# Revit family: Hager-Orion_Plus-IP65-D300-Cl.II-Poly_double_encl-630A-Floor_installation-CH-it
name_source: partatom
category: Electrical Equipment
units: mm (PartAtom-declared; Revit-internal decimal feet)

## family parameters
Cut with Voids When Loaded = No
Host = Face
Panel Configuration = Two Columns, Circuits Across
Part Type = Panelboard
Room Calculation Point = No
Round Connector Dimension = Use Diameter
Shared = No

## types (15) — shared parameters
EF000003 - Tipo di montaggio = EV012274 - montaggio a pavimento
EF000007 - colore = EV000270 - grigio
EF000049 - profondità = 300 mm  [stored 0.984252 ft]
EF000116 - numero RAL = 7035
EF001131 - profondità interna = 300 mm  [stored 0.984252 ft]
EF001596 - Attacco Lampada = EV000139 - plastica
EF001613 - Integrità del circuito = EV000494 - senza
EF005474 - grado di protezione (IP) = EV006421 - IP65
EF006306 - con serratura = Yes
EF007800 - adatto per parafulmine = No
EF008873 - corrente nominale (In) = 630 A
EF009170 - spessore materiale scatola = 2 mm  [stored 0.00656168 ft]
EF009171 - spessore materiale porta/coperchio = 2 mm  [stored 0.00656168 ft]
EF015940 - Coprire con rilascio di sovrapressione = No
HG000003 - Gamma = Orion Plus
HG000006 - Ad incasso = No
HG000010 - Porte asimmetriche = No
HG000023 - Custodia a doppia sezione = Yes
HG000024 - Altezza della sezione inferiore = 800 mm  [stored 2.62467 ft]
HG000026 - A pavimento = Yes
HG000027 - Altezza dello zoccolo = 70 mm  [stored 0.229659 ft]
Manufacturer = Hager
Type Comments = Orion Plus
zero-valued in all types: Default Elevation, EF000218 - profondità di incasso, EF000437 - numero di ingressi per conduttori, EF009554 - numero delle aperture per la piastra della flangia

## per-type parameters (varying)
| type | EF000008 - Larghezza | EF000040 - Altezza | EF000118 - con piastra di montaggio | EF000266 - numero di file | EF000339 - tipo di copertura | EF001088 - possibilità di applicazione | EF002950 - Numero moduli DIN | EF003532 - adatto per uso esterno | EF004293 - resistenza agli urti | EF004427 - numero di moduli | EF004464 - tipo di porta | EF006244 - coperchio/porta trasparente | EF009212 - esecuzione coperchio | HG000002 - Con porta | HG000004 - Codice produttore | HG000009 - Porta doppia a battente |
| montaggio a pavimento IP65 L1100 A1150 P300  - FL360B | 1100 mm | 1150 mm | No | 3 | EV004216 - porta | Yes | 0 | Yes | EV008784 - IK10 | 138 | EV002646 - singolo | Yes | EV009916 - con taglio | Yes | FL360B | Yes |
| montaggio a pavimento IP65 L1100 A1450 P300  - FL362B | 1100 mm | 1450 mm  [stored 4.75722 ft] | No | 3 | EV004216 - porta | Yes | 0 | Yes | EV008784 - IK10 | 138 | EV002646 - singolo | Yes | EV009916 - con taglio | Yes | FL362B | Yes |
| montaggio a pavimento IP65 L1100 A1750 P300  - FL364B | 1100 mm | 1750 mm  [stored 5.74147 ft] | No | 3 | EV004216 - porta | Yes | 0 | Yes | EV008784 - IK10 | 138 | EV002646 - singolo | Yes | EV009916 - con taglio | Yes | FL364B | Yes |
| montaggio a pavimento IP65 L1100 A1750 P300  - FL366B | 1100 mm | 1750 mm  [stored 5.74147 ft] | No | 5 | EV004216 - porta | Yes | 0 | Yes | EV008784 - IK10 | 230 | EV002646 - singolo | Yes | EV009916 - con taglio | Yes | FL366B | Yes |
| montaggio a pavimento IP65 L1100 A2050 P300  - FL368B | 1100 mm | 2050 mm  [stored 6.72572 ft] | Yes | 5 | EV001012 - coperchio | No | 0 | No | EV006814 - IK08 | 230 | EV002646 - singolo | No | EV000116 - chiuso | Yes | FL368B | Yes |
| montaggio a pavimento IP65 L600 A1150 P300  - FL340B | 600 mm | 1150 mm | No | 3 | EV004216 - porta | Yes | 0 | Yes | EV008784 - IK10 | 69 | EV002646 - singolo | Yes | EV009916 - con taglio | Yes | FL340B | No |
| montaggio a pavimento IP65 L600 A1450 P300  - FL342B | 600 mm | 1450 mm  [stored 4.75722 ft] | No | 3 | EV004216 - porta | Yes | 0 | Yes | EV008784 - IK10 | 69 | EV002646 - singolo | Yes | EV009916 - con taglio | No | FL342B | No |
| montaggio a pavimento IP65 L600 A1750 P300  - FL344B | 600 mm | 1750 mm  [stored 5.74147 ft] | No | 9 | EV004216 - porta | Yes | 23 | No |  | 0 |  | Yes | EV009916 - con taglio | Yes | FL344B | No |
| montaggio a pavimento IP65 L600 A1750 P300  - FL346B | 600 mm | 1750 mm  [stored 5.74147 ft] | No | 5 | EV004216 - porta | Yes | 0 | Yes | EV008784 - IK10 | 115 | EV002646 - singolo | Yes | EV009916 - con taglio | Yes | FL346B | No |
| montaggio a pavimento IP65 L600 A2050 P300  - FL348B | 600 mm | 2050 mm  [stored 6.72572 ft] | No | 3 | EV004216 - porta | Yes | 0 | Yes | EV008784 - IK10 | 115 | EV002646 - singolo | Yes | EV009916 - con taglio | Yes | FL348B | No |
| montaggio a pavimento IP65 L850 A1150 P300  - FL350B | 850 mm  [stored 2.78871 ft] | 1150 mm | No | 3 | EV004216 - porta | Yes | 0 | Yes | EV008784 - IK10 | 111 | EV002646 - singolo | Yes | EV009916 - con taglio | Yes | FL350B | No |
| montaggio a pavimento IP65 L850 A1450 P300  - FL352B | 850 mm  [stored 2.78871 ft] | 1450 mm  [stored 4.75722 ft] | Yes | 3 | EV001012 - coperchio | No | 0 | No | EV006814 - IK08 | 111 | EV002646 - singolo | No | EV000116 - chiuso | Yes | FL352B | No |
| montaggio a pavimento IP65 L850 A1750 P300  - FL354B | 850 mm  [stored 2.78871 ft] | 1750 mm  [stored 5.74147 ft] | Yes | 3 | EV001012 - coperchio | No | 0 | No | EV006814 - IK08 | 111 | EV002646 - singolo | No | EV000116 - chiuso | Yes | FL354B | No |
| montaggio a pavimento IP65 L850 A1750 P300  - FL356B | 850 mm  [stored 2.78871 ft] | 1750 mm  [stored 5.74147 ft] | No | 5 | EV004216 - porta | Yes | 0 | Yes | EV008784 - IK10 | 185 | EV002646 - singolo | Yes | EV009916 - con taglio | Yes | FL356B | No |
| montaggio a pavimento IP65 L850 A2050 P300  - FL358B | 850 mm  [stored 2.78871 ft] | 2050 mm  [stored 6.72572 ft] | No | 5 | EV004216 - porta | Yes | 0 | Yes | EV008784 - IK10 | 185 | EV002646 - singolo | Yes | EV009916 - con taglio | Yes | FL358B | No |

note: [stored X ft] marks values corroborated as IEEE doubles in the binary element streams (Revit-internal decimal feet)

## geometry (parser evidence)
native form markers: Sweep x10
no freeform markers — native parametric forms only
